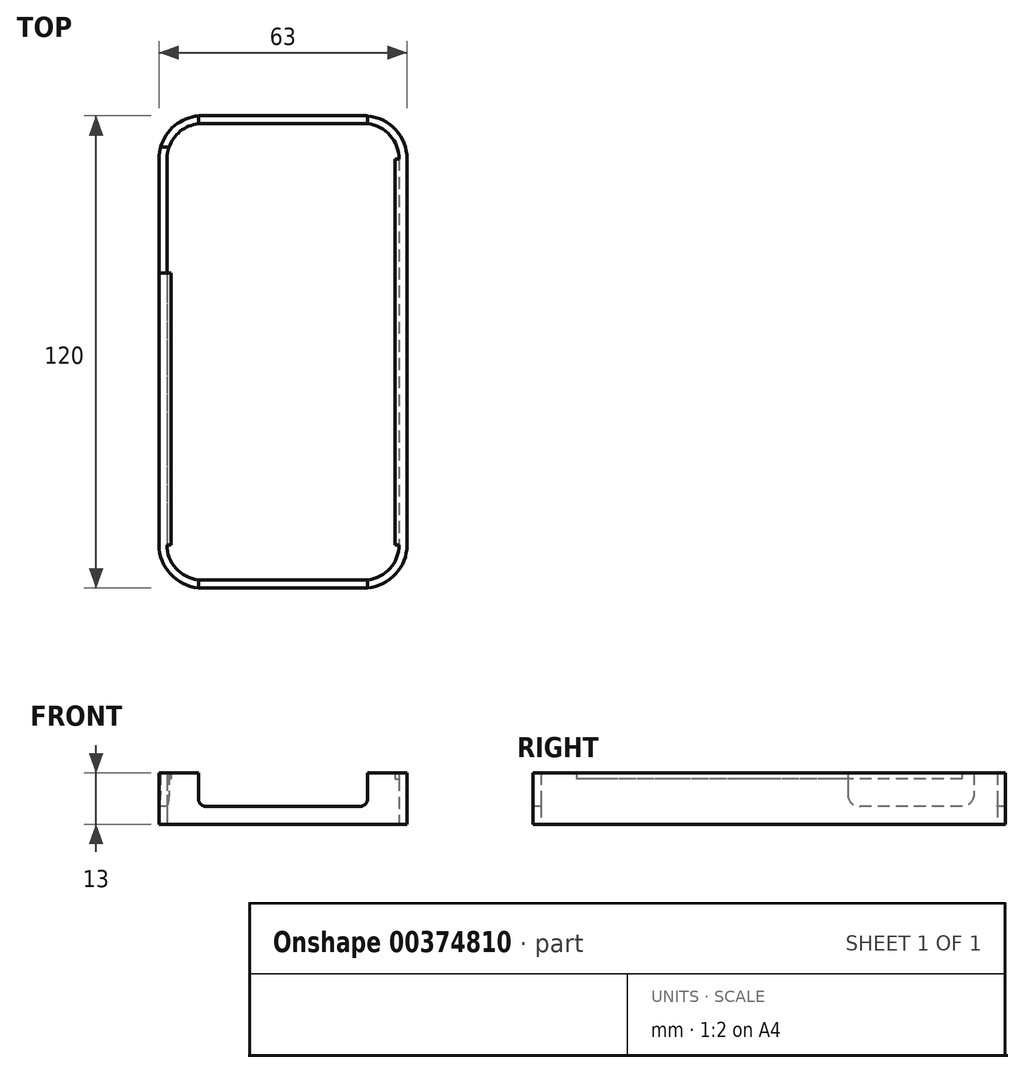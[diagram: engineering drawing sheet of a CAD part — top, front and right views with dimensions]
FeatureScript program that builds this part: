
annotation { "Feature Type Name" : "Feature", "Feature Type Description" : "" }
export const myFeature = defineFeature(function(context is Context, id is Id, definition is map)
    precondition{}
    {
        {
            var Q0;
            Q0=qCreatedBy(makeId("Top.planeOp"),FACE);
            var sketch = newSketch(context, id + "F0", { "sketchPlane" : qUnion([Q0])});
            skLineSegment(sketch, "E0.bottom", {"start": v(-23.03, 51.46) * mm, "end": v(17.97, 51.46) * mm});
            skLineSegment(sketch, "E0.top", {"start": v(-23.03, -68.54) * mm, "end": v(17.97, -68.54) * mm});
            skLineSegment(sketch, "E0.left", {"start": v(-34.03, 40.46) * mm, "end": v(-34.03, -57.54) * mm});
            skLineSegment(sketch, "E0.right", {"start": v(28.97, 40.46) * mm, "end": v(28.97, -57.54) * mm});
            skLineSegment(sketch, "E1.bottom", {"start": v(-23.03, 49.46) * mm, "end": v(17.97, 49.46) * mm});
            skLineSegment(sketch, "E1.top", {"start": v(-23.03, -66.54) * mm, "end": v(17.97, -66.54) * mm});
            skLineSegment(sketch, "E1.left", {"start": v(-32.03, 40.46) * mm, "end": v(-32.03, -57.54) * mm});
            skLineSegment(sketch, "E1.right", {"start": v(26.97, 40.46) * mm, "end": v(26.97, -57.54) * mm});
            skPoint(sketch, "E2.visualSharp", {"position": v(-34.03, 51.46) * mm});
            skArc(sketch, "E2.filletArc", {"start": v(-23.03, 51.46) * mm, "mid": v(-30.81, 48.24) * mm, "end": v(-34.03, 40.46) * mm});
            skPoint(sketch, "E3.visualSharp", {"position": v(28.97, 51.46) * mm});
            skArc(sketch, "E3.filletArc", {"start": v(28.97, 40.46) * mm, "mid": v(25.75, 48.24) * mm, "end": v(17.97, 51.46) * mm});
            skPoint(sketch, "E4.visualSharp", {"position": v(-34.03, -68.54) * mm});
            skArc(sketch, "E4.filletArc", {"start": v(-34.03, -57.54) * mm, "mid": v(-30.81, -65.32) * mm, "end": v(-23.03, -68.54) * mm});
            skPoint(sketch, "E5.visualSharp", {"position": v(28.97, -68.54) * mm});
            skArc(sketch, "E5.filletArc", {"start": v(17.97, -68.54) * mm, "mid": v(25.75, -65.32) * mm, "end": v(28.97, -57.54) * mm});
            skPoint(sketch, "E6.visualSharp", {"position": v(-32.03, 49.46) * mm});
            skArc(sketch, "E6.filletArc", {"start": v(-23.03, 49.46) * mm, "mid": v(-29.4, 46.82) * mm, "end": v(-32.03, 40.46) * mm});
            skPoint(sketch, "E7.visualSharp", {"position": v(26.97, 49.46) * mm});
            skArc(sketch, "E7.filletArc", {"start": v(26.97, 40.46) * mm, "mid": v(24.33, 46.82) * mm, "end": v(17.97, 49.46) * mm});
            skPoint(sketch, "E8.visualSharp", {"position": v(26.97, -66.54) * mm});
            skArc(sketch, "E8.filletArc", {"start": v(17.97, -66.54) * mm, "mid": v(24.33, -63.9) * mm, "end": v(26.97, -57.54) * mm});
            skPoint(sketch, "E9.visualSharp", {"position": v(-32.03, -66.54) * mm});
            skArc(sketch, "E9.filletArc", {"start": v(-32.03, -57.54) * mm, "mid": v(-29.4, -63.9) * mm, "end": v(-23.03, -66.54) * mm});
            skSolve(sketch);
        }
        {
            var Q0;
            Q0=qSketchRegion(id+"F0",true);
            extrude(context, id + "F1", {"entities" : qUnion([Q0]), "depth" : 13 * mm});
        }
        {
            var Q0;
            Q0=makeQuery(id+"F1.opExtrude","SWEPT_FACE",FACE,{"disambiguationData":[OSD([sQuery(id+"F0.wireOp",EDGE,"E0.left")])]});
            var sketch = newSketch(context, id + "F2", { "sketchPlane" : qUnion([Q0])});
            skLineSegment(sketch, "E10.bottom", {"start": v(-43.46, 13) * mm, "end": v(-11.46, 13) * mm});
            skLineSegment(sketch, "E10.top", {"start": v(-40.46, 4.5) * mm, "end": v(-14.46, 4.5) * mm});
            skLineSegment(sketch, "E10.left", {"start": v(-43.46, 13) * mm, "end": v(-43.46, 7.5) * mm});
            skLineSegment(sketch, "E10.right", {"start": v(-11.46, 13) * mm, "end": v(-11.46, 7.5) * mm});
            skPoint(sketch, "E11.visualSharp", {"position": v(-43.46, 4.5) * mm});
            skArc(sketch, "E11.filletArc", {"start": v(-43.46, 7.5) * mm, "mid": v(-42.58, 5.38) * mm, "end": v(-40.46, 4.5) * mm});
            skPoint(sketch, "E12.visualSharp", {"position": v(-11.46, 4.5) * mm});
            skArc(sketch, "E12.filletArc", {"start": v(-14.46, 4.5) * mm, "mid": v(-12.34, 5.38) * mm, "end": v(-11.46, 7.5) * mm});
            skSolve(sketch);
        }
        {
            var Q0;
            Q0=qSketchRegion(id+"F2",true);
            extrude(context, id + "F3", {"entities" : qUnion([Q0]), "operationType" : NewBodyOperationType.REMOVE, "endBound" : BoundingType.UP_TO_NEXT, "oppositeDirection" : true, "depth" : 25 * mm});
        }
        {
            var Q0;
            Q0=makeQuery(id+"F1.opExtrude","SWEPT_FACE",FACE,{"disambiguationData":[OSD([sQuery(id+"F0.wireOp",EDGE,"E0.top")])]});
            var sketch = newSketch(context, id + "F4", { "sketchPlane" : qUnion([Q0])});
            skLineSegment(sketch, "E13.bottom", {"start": v(-24.03, 13) * mm, "end": v(18.97, 13) * mm});
            skLineSegment(sketch, "E13.top", {"start": v(-22.03, 4.5) * mm, "end": v(16.97, 4.5) * mm});
            skLineSegment(sketch, "E13.left", {"start": v(-24.03, 13) * mm, "end": v(-24.03, 6.5) * mm});
            skLineSegment(sketch, "E13.right", {"start": v(18.97, 13) * mm, "end": v(18.97, 6.5) * mm});
            skPoint(sketch, "E14.visualSharp", {"position": v(-24.03, 4.5) * mm});
            skArc(sketch, "E14.filletArc", {"start": v(-24.03, 6.5) * mm, "mid": v(-23.45, 5.09) * mm, "end": v(-22.03, 4.5) * mm});
            skPoint(sketch, "E15.visualSharp", {"position": v(18.97, 4.5) * mm});
            skArc(sketch, "E15.filletArc", {"start": v(16.97, 4.5) * mm, "mid": v(18.38, 5.09) * mm, "end": v(18.97, 6.5) * mm});
            skSolve(sketch);
        }
        {
            var Q0;
            Q0=qSketchRegion(id+"F4",true);
            extrude(context, id + "F5", {"entities" : qUnion([Q0]), "operationType" : NewBodyOperationType.REMOVE, "endBound" : BoundingType.THROUGH_ALL, "oppositeDirection" : true, "depth" : 25 * mm});
        }
        {
            var Q0;
            Q0=makeQuery(id+"F1.opExtrude","SWEPT_FACE",FACE,{"disambiguationData":[OSD([sQuery(id+"F0.wireOp",EDGE,"E1.left")])]});
            var sketch = newSketch(context, id + "F6", { "sketchPlane" : qUnion([Q0])});
            skLineSegment(sketch, "E16.bottom", {"start": v(11.46, 13) * mm, "end": v(-57.54, 13) * mm});
            skLineSegment(sketch, "E16.top", {"start": v(11.46, 11.5) * mm, "end": v(-57.54, 11.5) * mm});
            skLineSegment(sketch, "E16.left", {"start": v(11.46, 13) * mm, "end": v(11.46, 11.5) * mm});
            skLineSegment(sketch, "E16.right", {"start": v(-57.54, 13) * mm, "end": v(-57.54, 11.5) * mm});
            skSolve(sketch);
        }
        {
            var Q0;
            Q0=qSketchRegion(id+"F6",true);
            extrude(context, id + "F7", {"entities" : qUnion([Q0]), "operationType" : NewBodyOperationType.ADD, "depth" : 1 * mm});
        }
        {
            var Q0;
            Q0=makeQuery(id+"F1.opExtrude","SWEPT_FACE",FACE,{"disambiguationData":[OSD([sQuery(id+"F0.wireOp",EDGE,"E1.right")])]});
            var sketch = newSketch(context, id + "F8", { "sketchPlane" : qUnion([Q0])});
            skLineSegment(sketch, "E17.bottom", {"start": v(-40.46, 13) * mm, "end": v(57.54, 13) * mm});
            skLineSegment(sketch, "E17.top", {"start": v(-40.46, 11.5) * mm, "end": v(57.54, 11.5) * mm});
            skLineSegment(sketch, "E17.left", {"start": v(-40.46, 13) * mm, "end": v(-40.46, 11.5) * mm});
            skLineSegment(sketch, "E17.right", {"start": v(57.54, 13) * mm, "end": v(57.54, 11.5) * mm});
            skSolve(sketch);
        }
        {
            var Q0;
            Q0=qSketchRegion(id+"F8",true);
            extrude(context, id + "F9", {"entities" : qUnion([Q0]), "operationType" : NewBodyOperationType.ADD, "depth" : 1 * mm});
        }
    });
